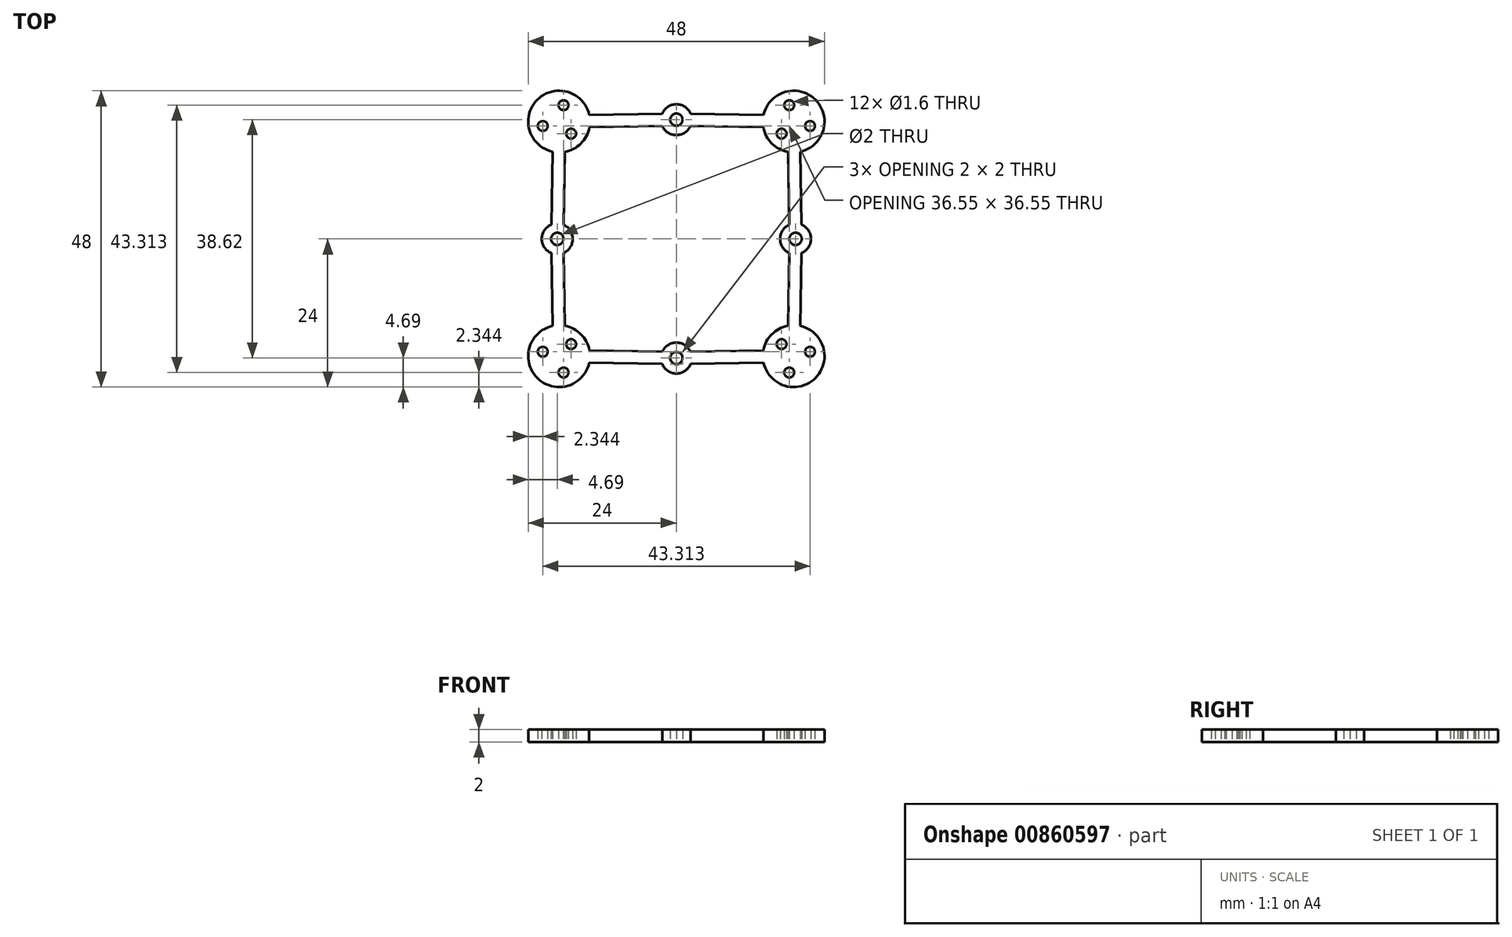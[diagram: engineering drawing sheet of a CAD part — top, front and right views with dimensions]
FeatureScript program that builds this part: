
annotation { "Feature Type Name" : "Feature", "Feature Type Description" : "" }
export const myFeature = defineFeature(function(context is Context, id is Id, definition is map)
    precondition{}
    {
        {
            var Q0;
            Q0=qCreatedBy(makeId("Top.planeOp"),FACE);
            var sketch = newSketch(context, id + "F0", { "sketchPlane" : qUnion([Q0])});
            skCircle(sketch, "E0", {"center": v(0, 11.3) * mm, "radius": 1 * mm});
            skCircle(sketch, "E1.1.0", {"center": v(-11.3, 0) * mm, "radius": 1 * mm});
            skCircle(sketch, "E1.2.0", {"center": v(0, -11.3) * mm, "radius": 1 * mm});
            skCircle(sketch, "E1.3.0", {"center": v(11.3, 0) * mm, "radius": 1 * mm});
            skPoint(sketch, "E1.center", {"position": v(0, 0) * mm});
            skPoint(sketch, "E2", {"position": v(19, 19) * mm});
            skCircle(sketch, "E3", {"center": v(17.06, 17.06) * mm, "radius": 0.8 * mm});
            skLineSegment(sketch, "E4", {"start": v(0, 0) * mm, "end": v(19, 19) * mm});
            skCircle(sketch, "E5.1.0", {"center": v(21.66, 18.29) * mm, "radius": 0.8 * mm});
            skCircle(sketch, "E5.2.0", {"center": v(18.29, 21.66) * mm, "radius": 0.8 * mm});
            skCircle(sketch, "E6", {"center": v(19, 19) * mm, "radius": 5 * mm});
            skCircle(sketch, "E7.1.0", {"center": v(-21.66, 18.29) * mm, "radius": 0.8 * mm});
            skCircle(sketch, "E7.1.1", {"center": v(-18.29, 21.66) * mm, "radius": 0.8 * mm});
            skCircle(sketch, "E7.1.2", {"center": v(-19, 19) * mm, "radius": 5 * mm});
            skCircle(sketch, "E7.1.3", {"center": v(-17.06, 17.06) * mm, "radius": 0.8 * mm});
            skCircle(sketch, "E7.2.0", {"center": v(-18.29, -21.66) * mm, "radius": 0.8 * mm});
            skCircle(sketch, "E7.2.1", {"center": v(-21.66, -18.29) * mm, "radius": 0.8 * mm});
            skCircle(sketch, "E7.2.2", {"center": v(-19, -19) * mm, "radius": 5 * mm});
            skCircle(sketch, "E7.2.3", {"center": v(-17.06, -17.06) * mm, "radius": 0.8 * mm});
            skCircle(sketch, "E7.3.0", {"center": v(21.66, -18.29) * mm, "radius": 0.8 * mm});
            skCircle(sketch, "E7.3.1", {"center": v(18.29, -21.66) * mm, "radius": 0.8 * mm});
            skCircle(sketch, "E7.3.2", {"center": v(19, -19) * mm, "radius": 5 * mm});
            skCircle(sketch, "E7.3.3", {"center": v(17.06, -17.06) * mm, "radius": 0.8 * mm});
            skCircle(sketch, "E8", {"center": v(0, 19.31) * mm, "radius": 1 * mm});
            skCircle(sketch, "E9", {"center": v(0, 19.31) * mm, "radius": 2.5 * mm});
            skCircle(sketch, "E10.1.0", {"center": v(-19.31, 0) * mm, "radius": 2.5 * mm});
            skCircle(sketch, "E10.1.1", {"center": v(-19.31, 0) * mm, "radius": 1 * mm});
            skCircle(sketch, "E10.2.0", {"center": v(0, -19.31) * mm, "radius": 2.5 * mm});
            skCircle(sketch, "E10.2.1", {"center": v(0, -19.31) * mm, "radius": 1 * mm});
            skCircle(sketch, "E10.3.0", {"center": v(19.31, 0) * mm, "radius": 2.5 * mm});
            skCircle(sketch, "E10.3.1", {"center": v(19.31, 0) * mm, "radius": 1 * mm});
            skLineSegment(sketch, "E11", {"start": v(-19, 19) * mm, "end": v(-19.3, 0) * mm});
            skLineSegment(sketch, "E12.0", {"start": v(-20, 19.02) * mm, "end": v(-20.28, 1.86) * mm});
            skLineSegment(sketch, "E13.0", {"start": v(-18, 18.98) * mm, "end": v(-18.28, 1.83) * mm});
            skLineSegment(sketch, "E14", {"start": v(-19.31, 0) * mm, "end": v(-19, -19) * mm});
            skLineSegment(sketch, "E15", {"start": v(-19, -19) * mm, "end": v(0, -19.31) * mm});
            skLineSegment(sketch, "E16", {"start": v(0, -19.31) * mm, "end": v(19, -19) * mm});
            skLineSegment(sketch, "E17", {"start": v(19.3, 0) * mm, "end": v(19, -19) * mm});
            skLineSegment(sketch, "E18", {"start": v(19.31, 0) * mm, "end": v(19, 19) * mm});
            skLineSegment(sketch, "E19", {"start": v(19, 19) * mm, "end": v(0, 19.3) * mm});
            skLineSegment(sketch, "E20", {"start": v(0, 19.31) * mm, "end": v(-19, 19) * mm});
            skLineSegment(sketch, "E21.0", {"start": v(-20.28, -1.86) * mm, "end": v(-19.98, -19.98) * mm});
            skLineSegment(sketch, "E21.1", {"start": v(-19.98, -19.98) * mm, "end": v(0, -20.31) * mm});
            skLineSegment(sketch, "E21.2", {"start": v(0, -20.31) * mm, "end": v(19.98, -19.98) * mm});
            skLineSegment(sketch, "E21.3", {"start": v(0, 20.31) * mm, "end": v(-19.02, 20) * mm});
            skLineSegment(sketch, "E21.4", {"start": v(19.98, 19.98) * mm, "end": v(0, 20.31) * mm});
            skLineSegment(sketch, "E21.5", {"start": v(20.31, 0) * mm, "end": v(19.98, 19.98) * mm});
            skLineSegment(sketch, "E21.6", {"start": v(20.31, 0) * mm, "end": v(19.98, -19.98) * mm});
            skLineSegment(sketch, "E22.0", {"start": v(-18.28, -1.83) * mm, "end": v(-18.02, -18.02) * mm});
            skLineSegment(sketch, "E22.1", {"start": v(-18.02, -18.02) * mm, "end": v(0, -18.3) * mm});
            skLineSegment(sketch, "E22.2", {"start": v(0, -18.3) * mm, "end": v(18.02, -18.02) * mm});
            skLineSegment(sketch, "E22.3", {"start": v(0, 18.3) * mm, "end": v(-18.98, 18) * mm});
            skLineSegment(sketch, "E22.4", {"start": v(18.02, 18.02) * mm, "end": v(0, 18.3) * mm});
            skLineSegment(sketch, "E22.5", {"start": v(18.3, 0) * mm, "end": v(18.02, 18.02) * mm});
            skLineSegment(sketch, "E22.6", {"start": v(18.3, 0) * mm, "end": v(18.02, -18.02) * mm});
            skSolve(sketch);
        }
        {
            var Q0;
            Q0 = qSketchRegion(id + "F0", true);
            var Q1;
            {var subQ0=sQuery(id+"F0.wireOp",EDGE,"E22.0");var subQ1=sQuery(id+"F0.wireOp",EDGE,"E7.2.2");var subQ2=makeQuery(id+"F0.imprint","INTERSECT",VERTEX,{"derivedFrom":[subQ1,subQ0]});Q1=makeQuery(id+"F0.imprint","IMPRINT",FACE,{"disambiguationData":[TD([[makeQuery(id+"F0.imprint","IMPRINT",EDGE,{"disambiguationData":[TD([[subQ2,-1.0]])],"derivedFrom":subQ1}),-1.0]])]});}
            var Q2;
            Q2=makeQuery(id+"F0.imprint","IMPRINT",FACE,{"disambiguationData":[TD([[makeQuery(id+"F0.imprint","IMPRINT",EDGE,{"derivedFrom":sQuery(id+"F0.wireOp",EDGE,"E7.2.3")}),-1.0]])]});
            var Q3;
            {var subQ0=sQuery(id+"F0.wireOp",EDGE,"E15");var subQ3=sQuery(id+"F0.wireOp",EDGE,"E7.2.2");var subQ4=makeQuery(id+"F0.imprint","INTERSECT",VERTEX,{"derivedFrom":[subQ3,subQ0]});Q3=makeQuery(id+"F0.imprint","IMPRINT",FACE,{"disambiguationData":[TD([[makeQuery(id+"F0.imprint","IMPRINT",EDGE,{"disambiguationData":[TD([[subQ4,-1.0]])],"derivedFrom":subQ3}),1.0]])]});}
            var Q4;
            {var subQ0=sQuery(id+"F0.wireOp",EDGE,"E15");var subQ1=sQuery(id+"F0.wireOp",EDGE,"E7.2.2");var subQ2=makeQuery(id+"F0.imprint","INTERSECT",VERTEX,{"derivedFrom":[subQ1,subQ0]});Q4=makeQuery(id+"F0.imprint","IMPRINT",FACE,{"disambiguationData":[TD([[makeQuery(id+"F0.imprint","IMPRINT",EDGE,{"disambiguationData":[TD([[subQ2,-1.0]])],"derivedFrom":subQ1}),-1.0]])]});}
            var Q5;
            {var subQ5=sQuery(id+"F0.wireOp",EDGE,"E10.1.0");var subQ9=makeQuery(id+"F0.imprint","INTERSECT",VERTEX,{"derivedFrom":[subQ5,sQuery(id+"F0.wireOp",EDGE,"E22.0")]});Q5=makeQuery(id+"F0.imprint","IMPRINT",FACE,{"disambiguationData":[TD([[makeQuery(id+"F0.imprint","IMPRINT",EDGE,{"disambiguationData":[TD([[subQ9,1.0]])],"derivedFrom":subQ5}),1.0]])]});}
            var Q6;
            {var subQ0=sQuery(id+"F0.wireOp",EDGE,"E11");var subQ1=sQuery(id+"F0.wireOp",EDGE,"E7.1.2");var subQ2=makeQuery(id+"F0.imprint","INTERSECT",VERTEX,{"derivedFrom":[subQ1,subQ0]});Q6=makeQuery(id+"F0.imprint","IMPRINT",FACE,{"disambiguationData":[TD([[makeQuery(id+"F0.imprint","IMPRINT",EDGE,{"disambiguationData":[TD([[subQ2,-1.0]])],"derivedFrom":subQ1}),-1.0]])]});}
            var Q7;
            {var subQ3=sQuery(id+"F0.wireOp",EDGE,"E7.1.2");var subQ6=sQuery(id+"F0.wireOp",EDGE,"E11");var subQ8=makeQuery(id+"F0.imprint","INTERSECT",VERTEX,{"derivedFrom":[subQ3,subQ6]});Q7=makeQuery(id+"F0.imprint","IMPRINT",FACE,{"disambiguationData":[TD([[makeQuery(id+"F0.imprint","IMPRINT",EDGE,{"disambiguationData":[TD([[subQ8,-1.0]])],"derivedFrom":subQ3}),1.0]])]});}
            var Q8;
            Q8=makeQuery(id+"F0.imprint","IMPRINT",FACE,{"disambiguationData":[TD([[makeQuery(id+"F0.imprint","IMPRINT",EDGE,{"derivedFrom":sQuery(id+"F0.wireOp",EDGE,"E7.1.3")}),-1.0]])]});
            var Q9;
            {var subQ0=sQuery(id+"F0.wireOp",EDGE,"E22.3");var subQ1=sQuery(id+"F0.wireOp",EDGE,"E7.1.2");var subQ2=makeQuery(id+"F0.imprint","INTERSECT",VERTEX,{"derivedFrom":[subQ1,subQ0]});Q9=makeQuery(id+"F0.imprint","IMPRINT",FACE,{"disambiguationData":[TD([[makeQuery(id+"F0.imprint","IMPRINT",EDGE,{"disambiguationData":[TD([[subQ2,-1.0]])],"derivedFrom":subQ1}),-1.0]])]});}
            var Q10;
            {var subQ0=sQuery(id+"F0.wireOp",EDGE,"E22.3");var subQ1=sQuery(id+"F0.wireOp",EDGE,"E9");var subQ2=makeQuery(id+"F0.imprint","INTERSECT",VERTEX,{"derivedFrom":[subQ1,subQ0]});Q10=makeQuery(id+"F0.imprint","IMPRINT",FACE,{"disambiguationData":[TD([[makeQuery(id+"F0.imprint","IMPRINT",EDGE,{"disambiguationData":[TD([[subQ2,-1.0]])],"derivedFrom":subQ1}),1.0]])]});}
            var Q11;
            {var subQ1=sQuery(id+"F0.wireOp",EDGE,"E8");var subQ10=sQuery(id+"F0.wireOp",EDGE,"E20");var subQ12=makeQuery(id+"F0.imprint","INTERSECT",VERTEX,{"derivedFrom":[subQ1,subQ10]});Q11=makeQuery(id+"F0.imprint","IMPRINT",FACE,{"disambiguationData":[TD([[makeQuery(id+"F0.imprint","IMPRINT",EDGE,{"disambiguationData":[TD([[subQ12,-1.0]])],"derivedFrom":subQ1}),-1.0]])]});}
            var Q12;
            {var subQ0=sQuery(id+"F0.wireOp",EDGE,"E19");var subQ1=sQuery(id+"F0.wireOp",EDGE,"E6");var subQ2=makeQuery(id+"F0.imprint","INTERSECT",VERTEX,{"derivedFrom":[subQ1,subQ0]});Q12=makeQuery(id+"F0.imprint","IMPRINT",FACE,{"disambiguationData":[TD([[makeQuery(id+"F0.imprint","IMPRINT",EDGE,{"disambiguationData":[TD([[subQ2,-1.0]])],"derivedFrom":subQ1}),-1.0]])]});}
            var Q13;
            {var subQ1=sQuery(id+"F0.wireOp",EDGE,"E4");var subQ3=sQuery(id+"F0.wireOp",EDGE,"E3");var subQ7=makeQuery(id+"F0.imprint","INTERSECT",VERTEX,{"disambiguationData":[OD(0.0)],"derivedFrom":[subQ3,subQ1]});Q13=makeQuery(id+"F0.imprint","IMPRINT",FACE,{"disambiguationData":[TD([[makeQuery(id+"F0.imprint","IMPRINT",EDGE,{"disambiguationData":[TD([[subQ7,1.0]])],"derivedFrom":subQ3}),-1.0]])]});}
            var Q14;
            {var subQ0=sQuery(id+"F0.wireOp",EDGE,"E19");var subQ5=sQuery(id+"F0.wireOp",EDGE,"E6");var subQ6=makeQuery(id+"F0.imprint","INTERSECT",VERTEX,{"derivedFrom":[subQ5,subQ0]});Q14=makeQuery(id+"F0.imprint","IMPRINT",FACE,{"disambiguationData":[TD([[makeQuery(id+"F0.imprint","IMPRINT",EDGE,{"disambiguationData":[TD([[subQ6,-1.0]])],"derivedFrom":subQ5}),1.0]])]});}
            var Q15;
            {var subQ1=sQuery(id+"F0.wireOp",EDGE,"E4");var subQ3=sQuery(id+"F0.wireOp",EDGE,"E3");var subQ7=makeQuery(id+"F0.imprint","INTERSECT",VERTEX,{"disambiguationData":[OD(0.0)],"derivedFrom":[subQ3,subQ1]});Q15=makeQuery(id+"F0.imprint","IMPRINT",FACE,{"disambiguationData":[TD([[makeQuery(id+"F0.imprint","IMPRINT",EDGE,{"disambiguationData":[TD([[subQ7,-1.0]])],"derivedFrom":subQ3}),-1.0]])]});}
            var Q16;
            {var subQ3=sQuery(id+"F0.wireOp",EDGE,"E22.5");var subQ5=sQuery(id+"F0.wireOp",EDGE,"E6");var subQ7=makeQuery(id+"F0.imprint","INTERSECT",VERTEX,{"derivedFrom":[subQ5,subQ3]});Q16=makeQuery(id+"F0.imprint","IMPRINT",FACE,{"disambiguationData":[TD([[makeQuery(id+"F0.imprint","IMPRINT",EDGE,{"disambiguationData":[TD([[subQ7,-1.0]])],"derivedFrom":subQ5}),1.0]])]});}
            var Q17;
            {var subQ0=sQuery(id+"F0.wireOp",EDGE,"E22.5");var subQ1=sQuery(id+"F0.wireOp",EDGE,"E6");var subQ2=makeQuery(id+"F0.imprint","INTERSECT",VERTEX,{"derivedFrom":[subQ1,subQ0]});Q17=makeQuery(id+"F0.imprint","IMPRINT",FACE,{"disambiguationData":[TD([[makeQuery(id+"F0.imprint","IMPRINT",EDGE,{"disambiguationData":[TD([[subQ2,-1.0]])],"derivedFrom":subQ1}),-1.0]])]});}
            var Q18;
            {var subQ0=sQuery(id+"F0.wireOp",EDGE,"E22.5");var subQ1=sQuery(id+"F0.wireOp",EDGE,"E10.3.0");var subQ2=makeQuery(id+"F0.imprint","INTERSECT",VERTEX,{"derivedFrom":[subQ1,subQ0]});Q18=makeQuery(id+"F0.imprint","IMPRINT",FACE,{"disambiguationData":[TD([[makeQuery(id+"F0.imprint","IMPRINT",EDGE,{"disambiguationData":[TD([[subQ2,-1.0]])],"derivedFrom":subQ1}),1.0]])]});}
            var Q19;
            {var subQ0=sQuery(id+"F0.wireOp",EDGE,"E18");var subQ1=sQuery(id+"F0.wireOp",EDGE,"E10.3.0");var subQ2=makeQuery(id+"F0.imprint","INTERSECT",VERTEX,{"derivedFrom":[subQ1,subQ0]});Q19=makeQuery(id+"F0.imprint","IMPRINT",FACE,{"disambiguationData":[TD([[makeQuery(id+"F0.imprint","IMPRINT",EDGE,{"disambiguationData":[TD([[subQ2,-1.0]])],"derivedFrom":subQ1}),1.0]])]});}
            var Q20;
            {var subQ0=sQuery(id+"F0.wireOp",EDGE,"E22.6");var subQ1=sQuery(id+"F0.wireOp",EDGE,"E10.3.0");var subQ2=makeQuery(id+"F0.imprint","INTERSECT",VERTEX,{"derivedFrom":[subQ1,subQ0]});Q20=makeQuery(id+"F0.imprint","IMPRINT",FACE,{"disambiguationData":[TD([[makeQuery(id+"F0.imprint","IMPRINT",EDGE,{"disambiguationData":[TD([[subQ2,-1.0]])],"derivedFrom":subQ1}),1.0]])]});}
            var Q21;
            {var subQ0=sQuery(id+"F0.wireOp",EDGE,"E17");var subQ1=sQuery(id+"F0.wireOp",EDGE,"E7.3.2");var subQ2=makeQuery(id+"F0.imprint","INTERSECT",VERTEX,{"derivedFrom":[subQ1,subQ0]});Q21=makeQuery(id+"F0.imprint","IMPRINT",FACE,{"disambiguationData":[TD([[makeQuery(id+"F0.imprint","IMPRINT",EDGE,{"disambiguationData":[TD([[subQ2,-1.0]])],"derivedFrom":subQ1}),-1.0]])]});}
            var Q22;
            Q22=makeQuery(id+"F0.imprint","IMPRINT",FACE,{"disambiguationData":[TD([[makeQuery(id+"F0.imprint","IMPRINT",EDGE,{"derivedFrom":sQuery(id+"F0.wireOp",EDGE,"E7.3.3")}),-1.0]])]});
            var Q23;
            {var subQ0=sQuery(id+"F0.wireOp",EDGE,"E17");var subQ3=sQuery(id+"F0.wireOp",EDGE,"E7.3.2");var subQ5=makeQuery(id+"F0.imprint","INTERSECT",VERTEX,{"derivedFrom":[subQ3,subQ0]});Q23=makeQuery(id+"F0.imprint","IMPRINT",FACE,{"disambiguationData":[TD([[makeQuery(id+"F0.imprint","IMPRINT",EDGE,{"disambiguationData":[TD([[subQ5,-1.0]])],"derivedFrom":subQ3}),1.0]])]});}
            var Q24;
            {var subQ0=sQuery(id+"F0.wireOp",EDGE,"E22.2");var subQ1=sQuery(id+"F0.wireOp",EDGE,"E7.3.2");var subQ2=makeQuery(id+"F0.imprint","INTERSECT",VERTEX,{"derivedFrom":[subQ1,subQ0]});Q24=makeQuery(id+"F0.imprint","IMPRINT",FACE,{"disambiguationData":[TD([[makeQuery(id+"F0.imprint","IMPRINT",EDGE,{"disambiguationData":[TD([[subQ2,-1.0]])],"derivedFrom":subQ1}),-1.0]])]});}
            var Q25;
            {var subQ0=sQuery(id+"F0.wireOp",EDGE,"E22.2");var subQ1=sQuery(id+"F0.wireOp",EDGE,"E10.2.0");var subQ2=makeQuery(id+"F0.imprint","INTERSECT",VERTEX,{"derivedFrom":[subQ1,subQ0]});Q25=makeQuery(id+"F0.imprint","IMPRINT",FACE,{"disambiguationData":[TD([[makeQuery(id+"F0.imprint","IMPRINT",EDGE,{"disambiguationData":[TD([[subQ2,-1.0]])],"derivedFrom":subQ1}),1.0]])]});}
            var Q26;
            {var subQ1=sQuery(id+"F0.wireOp",EDGE,"E10.2.0");var subQ5=sQuery(id+"F0.wireOp",EDGE,"E16");var subQ11=makeQuery(id+"F0.imprint","INTERSECT",VERTEX,{"derivedFrom":[subQ1,subQ5]});Q26=makeQuery(id+"F0.imprint","IMPRINT",FACE,{"disambiguationData":[TD([[makeQuery(id+"F0.imprint","IMPRINT",EDGE,{"disambiguationData":[TD([[subQ11,-1.0]])],"derivedFrom":subQ1}),1.0]])]});}
            extrude(context, id + "F1", {"entities" : qUnion([Q0, Q1, Q2, Q3, Q4, Q5, Q6, Q7, Q8, Q9, Q10, Q11, Q12, Q13, Q14, Q15, Q16, Q17, Q18, Q19, Q20, Q21, Q22, Q23, Q24, Q25, Q26]), "depth" : 2 * mm, "offsetDistance" : 25 * mm});
        }
    });
